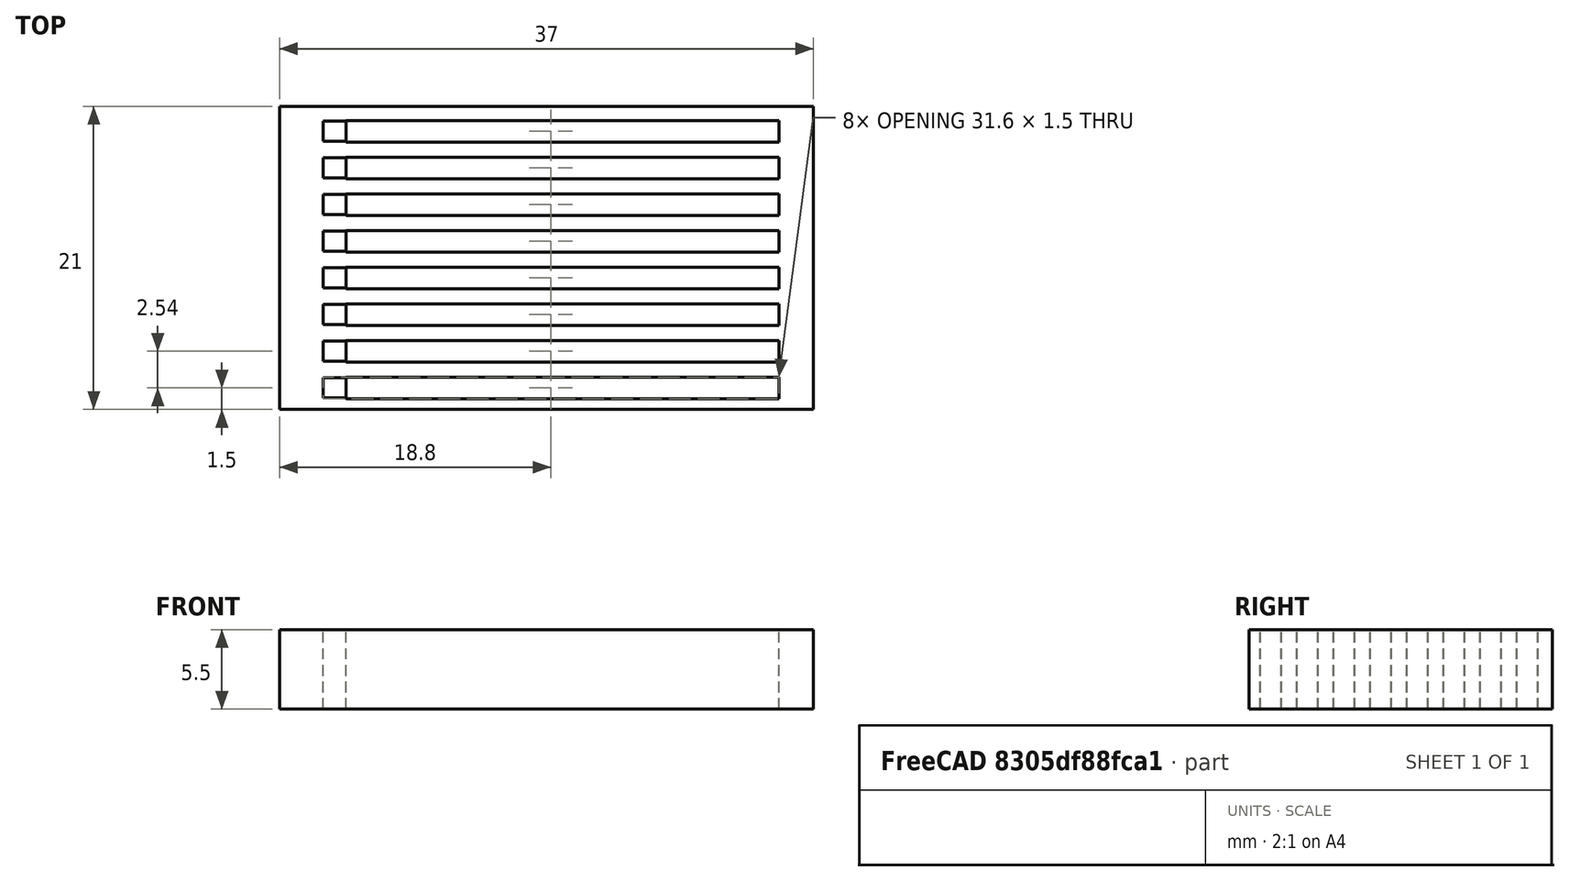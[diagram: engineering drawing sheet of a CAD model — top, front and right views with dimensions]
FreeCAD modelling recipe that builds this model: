
FCSTD DOCUMENT  (FreeCAD 0.17R13522 (Git))
Label: Test Piece V2 1.6
License: All rights reserved
LicenseURL: http://en.wikipedia.org/wiki/All_rights_reserved
objects: Part::Box×25, Part::MultiFuse×3, Part::Cut×2
note: 30 computed .brp shape members not serialized (recipe doc carries the construction recipe); baked Part::Feature solids carry a one-line shape summary decoded from their .brp

FEATURE [Part::Box] Box  label="Cube"
  AttacherType = Attacher::AttachEngine3D
  Height = 5.5
  Length = 37
  Width = 21
FEATURE [Part::Box] Box001  label="Cube001"
  AttacherType = Attacher::AttachEngine3D
  Height = 10
  Length = 1.6
  Placement = pos=(3,0.8,-3) rot=(0,0,1;0rad)
  Width = 1.4
FEATURE [Part::Box] Box002  label="Cube002"
  AttacherType = Attacher::AttachEngine3D
  Height = 10
  Length = 1.6
  Placement = pos=(3,3.34,-3) rot=(0,0,1;0rad)
  Width = 1.4
FEATURE [Part::Box] Box003  label="Cube003"
  AttacherType = Attacher::AttachEngine3D
  Height = 10
  Length = 1.6
  Placement = pos=(3,5.88,-3) rot=(0,0,1;0rad)
  Width = 1.4
FEATURE [Part::Box] Box004  label="Cube004"
  AttacherType = Attacher::AttachEngine3D
  Height = 10
  Length = 1.6
  Placement = pos=(3,8.42,-3) rot=(0,0,1;0rad)
  Width = 1.4
FEATURE [Part::Box] Box005  label="Cube005"
  AttacherType = Attacher::AttachEngine3D
  Height = 10
  Length = 1.6
  Placement = pos=(3,10.96,-3) rot=(0,0,1;0rad)
  Width = 1.4
FEATURE [Part::Box] Box006  label="Cube006"
  AttacherType = Attacher::AttachEngine3D
  Height = 10
  Length = 1.6
  Placement = pos=(3,13.5,-3) rot=(0,0,1;0rad)
  Width = 1.4
FEATURE [Part::Box] Box007  label="Cube007"
  AttacherType = Attacher::AttachEngine3D
  Height = 10
  Length = 1.6
  Placement = pos=(3,16.04,-3) rot=(0,0,1;0rad)
  Width = 1.4
FEATURE [Part::Box] Box008  label="Cube008"
  AttacherType = Attacher::AttachEngine3D
  Height = 10
  Length = 1.6
  Placement = pos=(3,18.58,-3) rot=(0,0,1;0rad)
  Width = 1.4
FEATURE [Part::Box] Box009  label="Cube009"
  AttacherType = Attacher::AttachEngine3D
  Height = 5.5
  Length = 30
  Placement = pos=(4.6,0.75,0) rot=(0,0,1;0rad)
  Width = 1.5
FEATURE [Part::Box] Box010  label="Cube010"
  AttacherType = Attacher::AttachEngine3D
  Height = 5.5
  Length = 30
  Placement = pos=(4.6,3.29,0) rot=(0,0,1;0rad)
  Width = 1.5
FEATURE [Part::Box] Box011  label="Cube011"
  AttacherType = Attacher::AttachEngine3D
  Height = 5.5
  Length = 30
  Placement = pos=(4.6,5.83,0) rot=(0,0,1;0rad)
  Width = 1.5
FEATURE [Part::Box] Box012  label="Cube012"
  AttacherType = Attacher::AttachEngine3D
  Height = 5.5
  Length = 30
  Placement = pos=(4.6,8.37,0) rot=(0,0,1;0rad)
  Width = 1.5
FEATURE [Part::Box] Box013  label="Cube013"
  AttacherType = Attacher::AttachEngine3D
  Height = 5.5
  Length = 30
  Placement = pos=(4.6,10.91,0) rot=(0,0,1;0rad)
  Width = 1.5
FEATURE [Part::Box] Box014  label="Cube014"
  AttacherType = Attacher::AttachEngine3D
  Height = 5.5
  Length = 30
  Placement = pos=(4.6,13.45,0) rot=(0,0,1;0rad)
  Width = 1.5
FEATURE [Part::Box] Box015  label="Cube015"
  AttacherType = Attacher::AttachEngine3D
  Height = 5.5
  Length = 30
  Placement = pos=(4.6,15.99,0) rot=(0,0,1;0rad)
  Width = 1.5
FEATURE [Part::Box] Box016  label="Cube016"
  AttacherType = Attacher::AttachEngine3D
  Height = 5.5
  Length = 30
  Placement = pos=(4.6,18.53,0) rot=(0,0,1;0rad)
  Width = 1.5
FEATURE [Part::MultiFuse] Fusion  label="Conducting Filament"
  Shapes = -> [Box009,Box010,Box011,Box012,Box013,Box014,Box015,Box016]
FEATURE [Part::MultiFuse] Fusion001
  Shapes = -> [Box001,Box002,Box003,Box004,Box005,Box006,Box007,Box008]
FEATURE [Part::Cut] Cut
  Base = -> Box
  Tool = -> Fusion001
FEATURE [Part::Box] Box017  label="Cube017"
  AttacherType = Attacher::AttachEngine3D
  Height = 5.5
  Length = 30
  Placement = pos=(4.6,0.75,0) rot=(0,0,1;0rad)
  Width = 1.5
FEATURE [Part::Box] Box018  label="Cube018"
  AttacherType = Attacher::AttachEngine3D
  Height = 5.5
  Length = 30
  Placement = pos=(4.6,10.91,0) rot=(0,0,1;0rad)
  Width = 1.5
FEATURE [Part::Box] Box019  label="Cube019"
  AttacherType = Attacher::AttachEngine3D
  Height = 5.5
  Length = 30
  Placement = pos=(4.6,3.29,0) rot=(0,0,1;0rad)
  Width = 1.5
FEATURE [Part::Box] Box020  label="Cube020"
  AttacherType = Attacher::AttachEngine3D
  Height = 5.5
  Length = 30
  Placement = pos=(4.6,5.83,0) rot=(0,0,1;0rad)
  Width = 1.5
FEATURE [Part::Box] Box021  label="Cube021"
  AttacherType = Attacher::AttachEngine3D
  Height = 5.5
  Length = 30
  Placement = pos=(4.6,18.53,0) rot=(0,0,1;0rad)
  Width = 1.5
FEATURE [Part::Box] Box022  label="Cube022"
  AttacherType = Attacher::AttachEngine3D
  Height = 5.5
  Length = 30
  Placement = pos=(4.6,15.99,0) rot=(0,0,1;0rad)
  Width = 1.5
FEATURE [Part::Box] Box023  label="Cube023"
  AttacherType = Attacher::AttachEngine3D
  Height = 5.5
  Length = 30
  Placement = pos=(4.6,8.37,0) rot=(0,0,1;0rad)
  Width = 1.5
FEATURE [Part::Box] Box024  label="Cube024"
  AttacherType = Attacher::AttachEngine3D
  Height = 5.5
  Length = 30
  Placement = pos=(4.6,13.45,0) rot=(0,0,1;0rad)
  Width = 1.5
FEATURE [Part::MultiFuse] Fusion002
  Shapes = -> [Box017,Box018,Box019,Box020,Box021,Box022,Box023,Box024]
FEATURE [Part::Cut] Cut001  label="Main body"
  Base = -> Cut
  Tool = -> Fusion002
